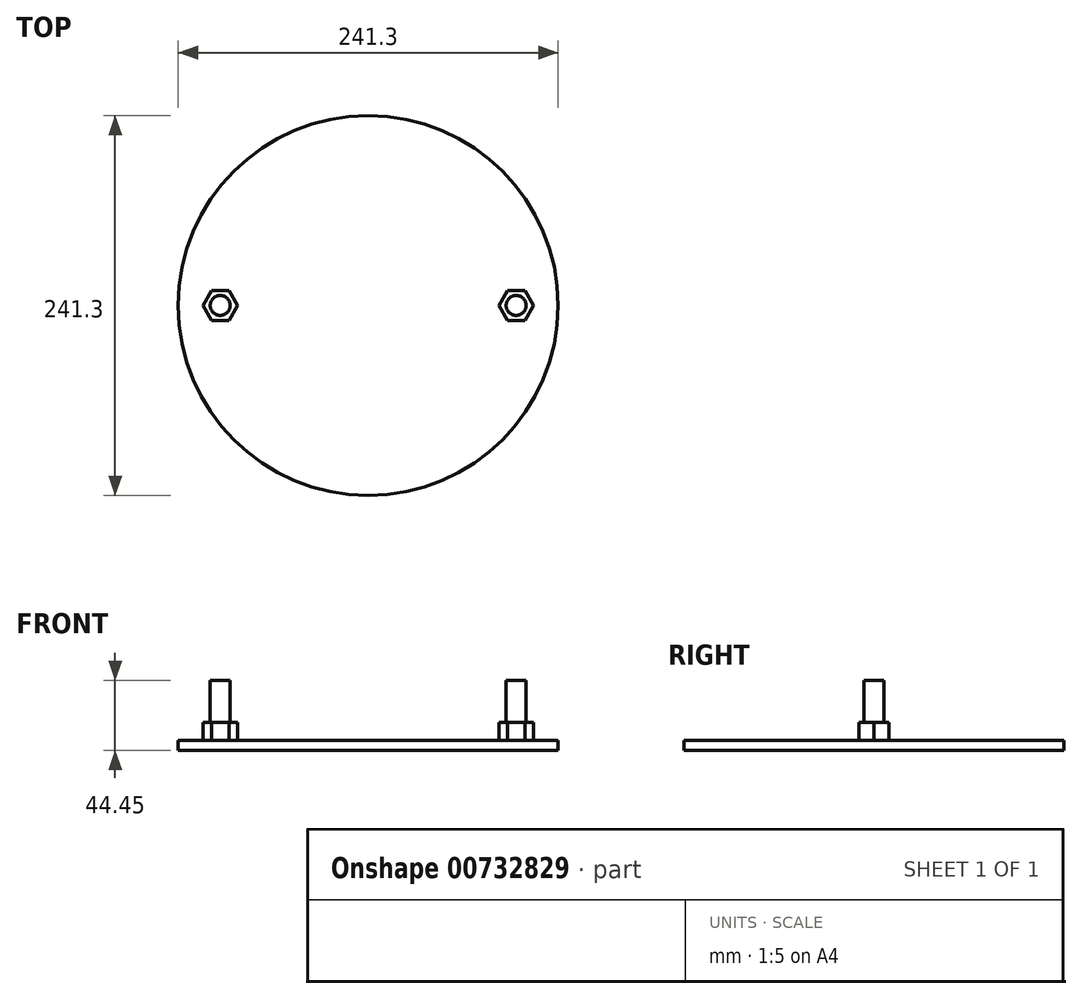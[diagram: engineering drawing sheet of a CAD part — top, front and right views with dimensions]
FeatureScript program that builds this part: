
annotation { "Feature Type Name" : "Feature", "Feature Type Description" : "" }
export const myFeature = defineFeature(function(context is Context, id is Id, definition is map)
    precondition{}
    {
        {
            var Q0;
            Q0=qCreatedBy(makeId("Top.planeOp"),FACE);
            var sketch = newSketch(context, id + "F0", { "sketchPlane" : qUnion([Q0])});
            skCircle(sketch, "E0", {"center": v(0, 0) * mm, "radius": 120.65 * mm});
            skSolve(sketch);
        }
        {
            var Q0;
            Q0=makeQuery(id+"F0.imprint","IMPRINT",FACE,{"disambiguationData":[TD([[makeQuery(id+"F0.imprint","IMPRINT",EDGE,{"derivedFrom":sQuery(id+"F0.wireOp",EDGE,"E0")}),1.0]])]});
            extrude(context, id + "F1", {"entities" : qUnion([Q0]), "depth" : 6.35 * mm, "offsetDistance" : 25.4 * mm});
        }
        {
            var Q0;
            Q0=makeQuery(id+"F1.opExtrude","CAP_FACE",FACE,{"disambiguationData":[OSD([sQuery(id+"F0.wireOp",EDGE,"E0")])],"isStart":false});
            var sketch = newSketch(context, id + "F2", { "sketchPlane" : qUnion([Q0])});
            skLineSegment(sketch, "E1", {"start": v(-215.7, 0) * mm, "end": v(211.27, 0) * mm, "construction": true});
            skCircle(sketch, "E2", {"center": v(-93.98, 0) * mm, "radius": 6.35 * mm});
            skCircle(sketch, "E3", {"center": v(93.98, 0) * mm, "radius": 6.35 * mm});
            skSolve(sketch);
        }
        {
            var Q0;
            Q0 = qSketchRegion(id + "F2", true);
            extrude(context, id + "F3", {"entities" : qUnion([Q0]), "operationType" : NewBodyOperationType.ADD, "depth" : 38.1 * mm, "offsetDistance" : 25.4 * mm});
        }
        {
            var Q0;
            Q0=makeQuery(id+"F1.opExtrude","CAP_FACE",FACE,{"disambiguationData":[OSD([sQuery(id+"F0.wireOp",EDGE,"E0")])],"isStart":false});
            var sketch = newSketch(context, id + "F4", { "sketchPlane" : qUnion([Q0])});
            skCircle(sketch, "E4.cCircle", {"center": v(-93.98, 0) * mm, "radius": 9.52 * mm, "construction": true});
            skLineSegment(sketch, "E4.0", {"start": v(-99.48, 9.52) * mm, "end": v(-88.48, 9.52) * mm});
            skLineSegment(sketch, "E4.1", {"start": v(-88.48, 9.52) * mm, "end": v(-82.98, 0) * mm});
            skLineSegment(sketch, "E4.2", {"start": v(-82.98, 0) * mm, "end": v(-88.48, -9.53) * mm});
            skLineSegment(sketch, "E4.3", {"start": v(-88.48, -9.53) * mm, "end": v(-99.48, -9.53) * mm});
            skLineSegment(sketch, "E4.4", {"start": v(-99.48, -9.53) * mm, "end": v(-104.98, 0) * mm});
            skLineSegment(sketch, "E4.5", {"start": v(-104.98, 0) * mm, "end": v(-99.48, 9.52) * mm});
            skPoint(sketch, "E4.0.midPoint", {"position": v(-93.98, 9.52) * mm});
            skCircle(sketch, "E5.cCircle", {"center": v(93.98, 0) * mm, "radius": 9.53 * mm, "construction": true});
            skLineSegment(sketch, "E5.0", {"start": v(88.48, 9.52) * mm, "end": v(99.48, 9.52) * mm});
            skLineSegment(sketch, "E5.1", {"start": v(99.48, 9.52) * mm, "end": v(104.98, 0) * mm});
            skLineSegment(sketch, "E5.2", {"start": v(104.98, 0) * mm, "end": v(99.48, -9.53) * mm});
            skLineSegment(sketch, "E5.3", {"start": v(99.48, -9.53) * mm, "end": v(88.48, -9.53) * mm});
            skLineSegment(sketch, "E5.4", {"start": v(88.48, -9.53) * mm, "end": v(82.98, 0) * mm});
            skLineSegment(sketch, "E5.5", {"start": v(82.98, 0) * mm, "end": v(88.48, 9.52) * mm});
            skPoint(sketch, "E5.0.midPoint", {"position": v(93.98, 9.52) * mm});
            skSolve(sketch);
        }
        {
            var Q0;
            Q0=makeQuery(id+"F4.imprint","IMPRINT",FACE,{"disambiguationData":[TD([[makeQuery(id+"F4.imprint","IMPRINT",EDGE,{"derivedFrom":sQuery(id+"F4.wireOp",EDGE,"E4.0")}),-1.0]])]});
            var Q1;
            Q1=makeQuery(id+"F4.imprint","IMPRINT",FACE,{"disambiguationData":[TD([[makeQuery(id+"F4.imprint","IMPRINT",EDGE,{"derivedFrom":sQuery(id+"F4.wireOp",EDGE,"E5.0")}),-1.0]])]});
            extrude(context, id + "F5", {"entities" : qUnion([Q0, Q1]), "operationType" : NewBodyOperationType.ADD, "depth" : 11.38 * mm, "offsetDistance" : 25.4 * mm});
        }
    });
